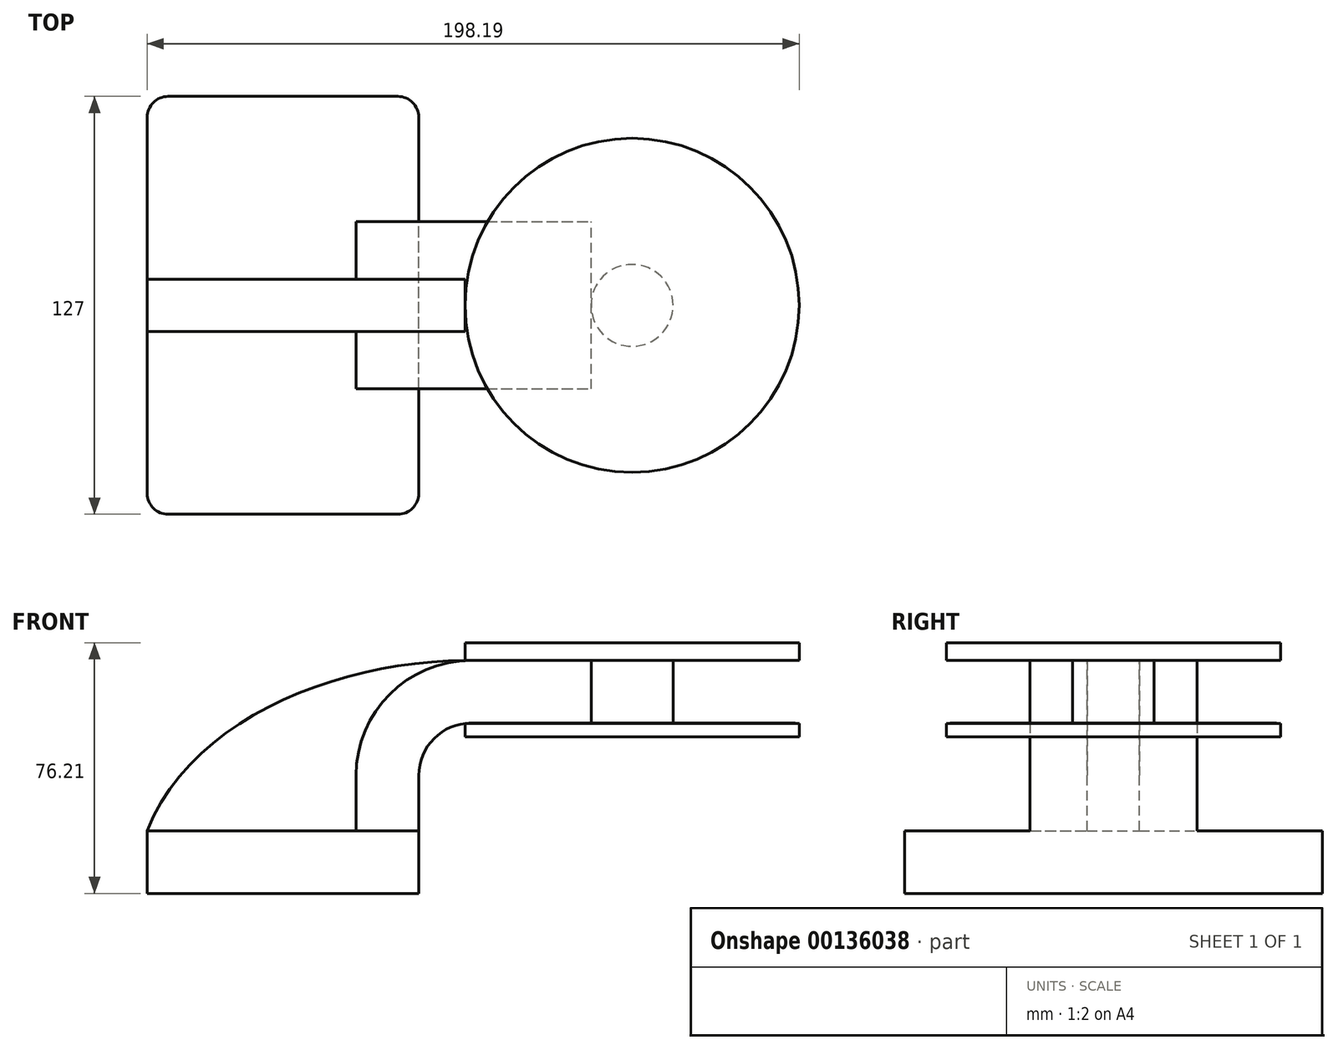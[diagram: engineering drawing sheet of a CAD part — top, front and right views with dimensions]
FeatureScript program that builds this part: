
annotation { "Feature Type Name" : "Feature", "Feature Type Description" : "" }
export const myFeature = defineFeature(function(context is Context, id is Id, definition is map)
    precondition{}
    {
        {
            var Q0;
            Q0=qCreatedBy(makeId("Front.planeOp"),FACE);
            var sketch = newSketch(context, id + "F0", { "sketchPlane" : qUnion([Q0])});
            skLineSegment(sketch, "E0.bottom", {"start": v(41.27, 9.53) * mm, "end": v(-41.28, 9.53) * mm});
            skLineSegment(sketch, "E0.top", {"start": v(41.28, -9.52) * mm, "end": v(-41.27, -9.52) * mm});
            skLineSegment(sketch, "E0.left", {"start": v(41.28, 9.53) * mm, "end": v(41.28, -9.52) * mm});
            skLineSegment(sketch, "E0.right", {"start": v(-41.28, 9.53) * mm, "end": v(-41.27, -9.52) * mm});
            skPoint(sketch, "E0.middle", {"position": v(0, 0) * mm});
            skLineSegment(sketch, "E1.bottom", {"start": v(55.31, 38.1) * mm, "end": v(106.11, 38.1) * mm});
            skLineSegment(sketch, "E1.top", {"start": v(55.31, 66.68) * mm, "end": v(106.11, 66.68) * mm});
            skLineSegment(sketch, "E1.left", {"start": v(55.31, 38.1) * mm, "end": v(55.31, 66.68) * mm});
            skLineSegment(sketch, "E1.right", {"start": v(106.11, 38.1) * mm, "end": v(106.11, 66.68) * mm});
            skPoint(sketch, "E1.middle", {"position": v(80.71, 52.39) * mm});
            skLineSegment(sketch, "E2", {"start": v(41.27, 9.53) * mm, "end": v(41.27, 26.31) * mm});
            skLineSegment(sketch, "E3", {"start": v(15916.28, 15901.48) * mm, "end": v(15934.7, 15901.48) * mm});
            skArc(sketch, "E4", {"start": v(41.27, 26.31) * mm, "mid": v(45.92, 37.54) * mm, "end": v(57.15, 42.19) * mm});
            skLineSegment(sketch, "E5", {"start": v(57.15, 42.19) * mm, "end": v(93.68, 42.19) * mm});
            skArc(sketch, "E6.0", {"start": v(47.62, 26.31) * mm, "mid": v(50.41, 33.05) * mm, "end": v(57.15, 35.84) * mm});
            skLineSegment(sketch, "E7.0", {"start": v(57.15, 61.24) * mm, "end": v(93.68, 61.24) * mm});
            skArc(sketch, "E7.1", {"start": v(22.23, 26.31) * mm, "mid": v(32.45, 51.01) * mm, "end": v(57.15, 61.24) * mm});
            skLineSegment(sketch, "E7.2", {"start": v(22.23, 9.53) * mm, "end": v(22.23, 26.31) * mm});
            skLineSegment(sketch, "E8", {"start": v(93.68, 42.19) * mm, "end": v(93.68, 61.24) * mm});
            skFitSpline(sketch, "E9", {"points": [v(-41.28, 9.53) * mm, v(57.15, 61.24) * mm], "startDerivative": vector(41.37, 105.27) * mm, "endDerivative": vector(115.77, -0.73) * mm});
            skSolve(sketch);
        }
        {
            var Q0;
            Q0=makeQuery(id+"F0.imprint","IMPRINT",FACE,{"disambiguationData":[TD([[makeQuery(id+"F0.imprint","IMPRINT",EDGE,{"derivedFrom":sQuery(id+"F0.wireOp",EDGE,"E0.top")}),-1.0]])]});
            extrude(context, id + "F1", {"entities" : qUnion([Q0]), "endBound" : BoundingType.SYMMETRIC, "depth" : 127 * mm});
        }
        {
            var Q0;
            {var subQ1=sQuery(id+"F0.wireOp",EDGE,"E2");Q0=makeQuery(id+"F0.imprint","IMPRINT",FACE,{"disambiguationData":[TD([[makeQuery(id+"F0.imprint","IMPRINT",EDGE,{"derivedFrom":subQ1}),1.0]])]});}
            var Q1;
            {var subQ1=sQuery(id+"F0.wireOp",EDGE,"E5");Q1=makeQuery(id+"F0.imprint","IMPRINT",FACE,{"disambiguationData":[TD([[makeQuery(id+"F0.imprint","IMPRINT",EDGE,{"derivedFrom":subQ1}),1.0]])]});}
            extrude(context, id + "F2", {"entities" : qUnion([Q0, Q1]), "operationType" : NewBodyOperationType.ADD, "endBound" : BoundingType.SYMMETRIC, "depth" : 50.8 * mm});
        }
        {
            var Q0;
            {var subQ0=sQuery(id+"F0.wireOp",EDGE,"E7.2");Q0=makeQuery(id+"F0.imprint","IMPRINT",FACE,{"disambiguationData":[TD([[makeQuery(id+"F0.imprint","IMPRINT",EDGE,{"derivedFrom":subQ0}),1.0]])]});}
            extrude(context, id + "F3", {"entities" : qUnion([Q0]), "operationType" : NewBodyOperationType.ADD, "endBound" : BoundingType.SYMMETRIC, "depth" : 15.88 * mm});
        }
        {
            var Q0;
            {var subQ4=sQuery(id+"F0.wireOp",EDGE,"E1.bottom");Q0=makeQuery(id+"F0.imprint","IMPRINT",FACE,{"disambiguationData":[TD([[makeQuery(id+"F0.imprint","IMPRINT",EDGE,{"derivedFrom":subQ4}),1.0]])]});}
            var Q1;
            Q1=sQuery(id+"F0.wireOp",EDGE,"E1.right");
            revolve(context, id + "F4", {"entities" : qUnion([Q0]), "axis" : qUnion([Q1]), "revolveType" : RevolveType.FULL});
        }
        {
            var Q0;
            Q0=makeQuery(id+"F1.opExtrude","CAP_EDGE",EDGE,{"disambiguationData":[OSD([sQuery(id+"F0.wireOp",EDGE,"E0.left")])],"isStart":false});
            var Q1;
            Q1=makeQuery(id+"F1.opExtrude","CAP_EDGE",EDGE,{"disambiguationData":[OSD([sQuery(id+"F0.wireOp",EDGE,"E0.right")])],"isStart":false});
            var Q2;
            Q2=makeQuery(id+"F1.opExtrude","CAP_EDGE",EDGE,{"disambiguationData":[OSD([sQuery(id+"F0.wireOp",EDGE,"E0.left")])],"isStart":true});
            var Q3;
            Q3=makeQuery(id+"F1.opExtrude","CAP_EDGE",EDGE,{"disambiguationData":[OSD([sQuery(id+"F0.wireOp",EDGE,"E0.right")])],"isStart":true});
            fillet(context, id + "F5", {"entities" : qUnion([Q0, Q1, Q2, Q3]), "radius" : 6.35 * mm, "tangentPropagation" : true, "allowEdgeOverflow" : false});
        }
    });
